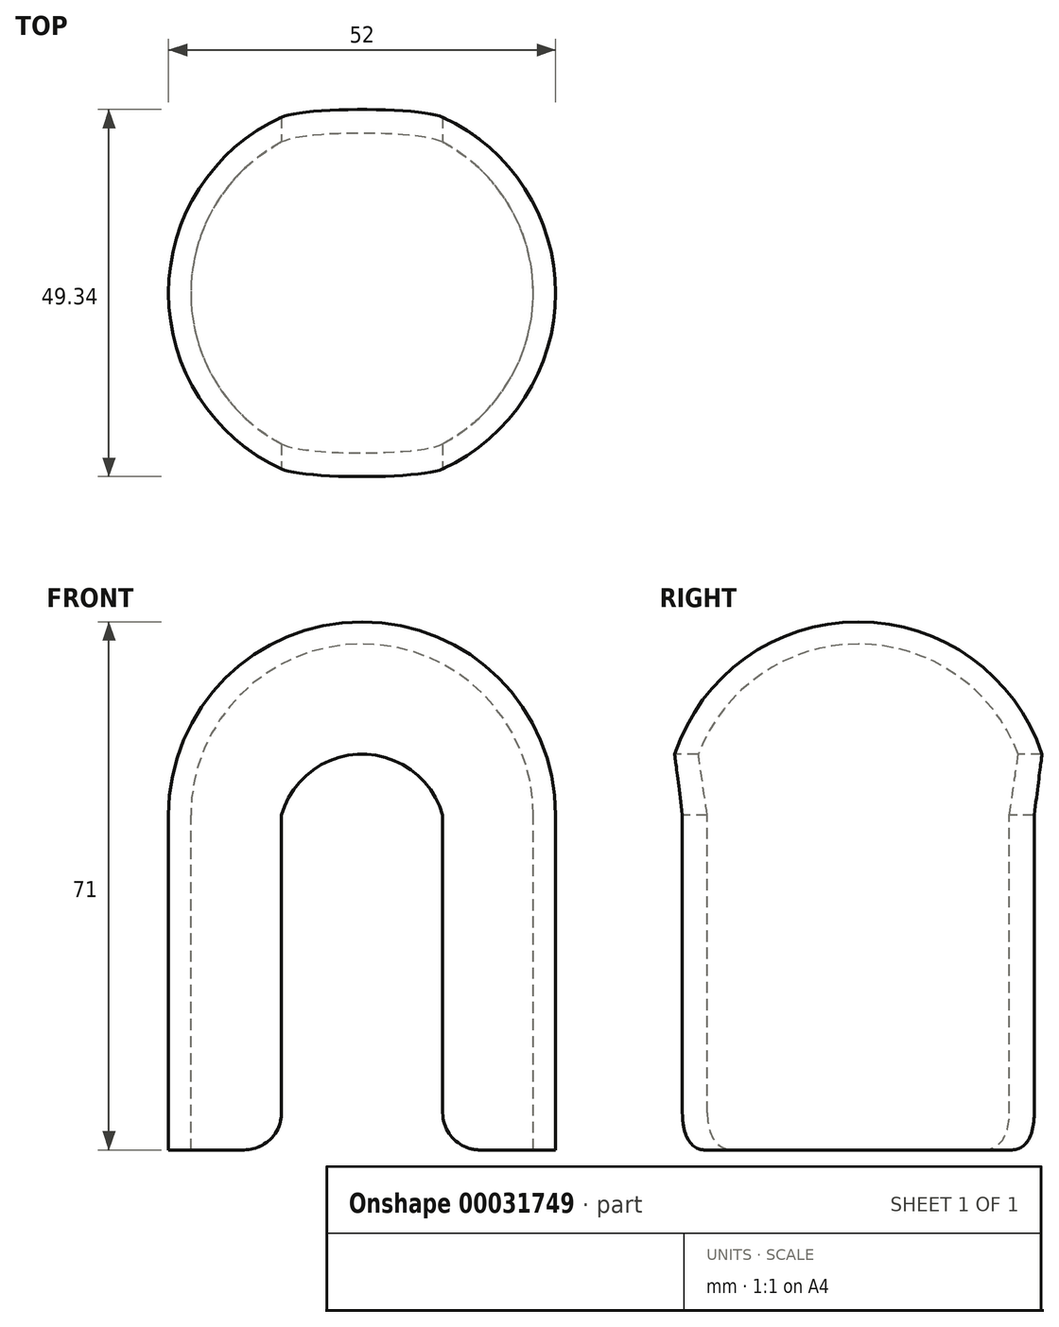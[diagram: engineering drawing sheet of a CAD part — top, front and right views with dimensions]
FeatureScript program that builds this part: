
annotation { "Feature Type Name" : "Feature", "Feature Type Description" : "" }
export const myFeature = defineFeature(function(context is Context, id is Id, definition is map)
    precondition{}
    {
        {
            var Q0;
            Q0=qCreatedBy(makeId("Top.planeOp"),FACE);
            var sketch = newSketch(context, id + "F0", { "sketchPlane" : qUnion([Q0])});
            skLineSegment(sketch, "E0", {"start": v(0, 26) * mm, "end": v(0, -26) * mm});
            skArc(sketch, "E1", {"start": v(0, -26) * mm, "mid": v(26, 0) * mm, "end": v(0, 26) * mm});
            skLineSegment(sketch, "E2", {"start": v(0, 0) * mm, "end": v(24.2, 0) * mm, "construction": true});
            skSolve(sketch);
        }
        {
            var Q0;
            Q0=makeQuery(id+"F0.imprint","IMPRINT",FACE,{"disambiguationData":[TD([[makeQuery(id+"F0.imprint","IMPRINT",EDGE,{"derivedFrom":sQuery(id+"F0.wireOp",EDGE,"E0")}),1.0]])]});
            var Q1;
            Q1=sQuery(id+"F0.wireOp",EDGE,"E0");
            revolve(context, id + "F1", {"entities" : qUnion([Q0]), "axis" : qUnion([Q1]), "revolveType" : RevolveType.ONE_DIRECTION, "angle" : 180 * degree});
        }
        {
            var Q0;
            Q0=qCreatedBy(makeId("Top.planeOp"),FACE);
            var sketch = newSketch(context, id + "F2", { "sketchPlane" : qUnion([Q0])});
            skArc(sketch, "E3", {"start": v(0, -23) * mm, "mid": v(23, 0) * mm, "end": v(0, 23) * mm});
            skLineSegment(sketch, "E4", {"start": v(0, -23) * mm, "end": v(0, 23) * mm});
            skSolve(sketch);
        }
        {
            var Q0;
            Q0 = qSketchRegion(id + "F2", true);
            var Q1;
            Q1=sQuery(id+"F2.wireOp",EDGE,"E4");
            revolve(context, id + "F3", {"operationType" : NewBodyOperationType.REMOVE, "entities" : qUnion([Q0]), "axis" : qUnion([Q1]), "revolveType" : RevolveType.FULL, "oppositeDirection" : true});
        }
        {
            var Q0;
            Q0=qCreatedBy(makeId("Front.planeOp"),FACE);
            cPlane(context, id + "F4", {"entities" : qUnion([Q0]), "cplaneType" : CPlaneType.OFFSET, "offset" : 24.27 * mm, "width" : 150 * mm, "height" : 150 * mm});
        }
        {
            var Q0;
            Q0=qCreatedBy(id+"F4.planeOp",FACE);
            var sketch = newSketch(context, id + "F5", { "sketchPlane" : qUnion([Q0])});
            skCircle(sketch, "E5", {"center": v(0, -3.05) * mm, "radius": 11.25 * mm});
            skArc(sketch, "E6", {"start": v(26, 0) * mm, "mid": v(0, 26) * mm, "end": v(-26, 0) * mm});
            skLineSegment(sketch, "E7", {"start": v(-10.83, 0) * mm, "end": v(10.83, 0) * mm, "construction": true});
            skSolve(sketch);
        }
        {
            var Q0;
            Q0 = qSketchRegion(id + "F5", true);
            extrude(context, id + "F6", {"entities" : qUnion([Q0]), "operationType" : NewBodyOperationType.REMOVE, "oppositeDirection" : true, "depth" : 62.58 * mm, "hasSecondDirection" : true, "secondDirectionOppositeDirection" : false, "secondDirectionDepth" : 22.8 * mm});
        }
        {
            var Q0;
            Q0=makeQuery(id+"F6.boolean.opBoolean","SPLIT",FACE,{"disambiguationData":[OD(1.0)],"derivedFrom":makeQuery(id+"F1.opRevolve","CAP_FACE",FACE,{"disambiguationData":[OSD([sQuery(id+"F0.wireOp",EDGE,"E0"),sQuery(id+"F0.wireOp",EDGE,"E1")])],"isStart":true})});
            var Q1;
            Q1=makeQuery(id+"F6.boolean.opBoolean","SPLIT",FACE,{"disambiguationData":[OD(0.0)],"derivedFrom":makeQuery(id+"F1.opRevolve","CAP_FACE",FACE,{"disambiguationData":[OSD([sQuery(id+"F0.wireOp",EDGE,"E0"),sQuery(id+"F0.wireOp",EDGE,"E1")])],"isStart":true})});
            extrude(context, id + "F7", {"entities" : qUnion([Q0, Q1]), "operationType" : NewBodyOperationType.ADD, "depth" : 45 * mm});
        }
        {
            var Q0;
            {var subQ0=sQuery(id+"F0.wireOp",EDGE,"E0");var subQ1=sQuery(id+"F0.wireOp",EDGE,"E1");var subQ2=sQuery(id+"F5.wireOp",EDGE,"E5");Q0=makeQuery(id+"F7.opExtrude","CAP_EDGE",EDGE,{"disambiguationData":[OSD([subQ0,subQ1,subQ2]),TDD([makeQuery(id+"F6.boolean.opBoolean","INTERSECT",EDGE,{"disambiguationData":[OD(1.0)],"derivedFrom":[makeQuery(id+"F1.opRevolve","CAP_FACE",FACE,{"disambiguationData":[OSD([subQ0,subQ1])],"isStart":true}),makeQuery(id+"F6.opExtrude","SWEPT_FACE",FACE,{"disambiguationData":[OSD([subQ2])]})]})])],"isStart":false});}
            var Q1;
            {var subQ0=sQuery(id+"F0.wireOp",EDGE,"E0");var subQ1=sQuery(id+"F0.wireOp",EDGE,"E1");var subQ2=sQuery(id+"F5.wireOp",EDGE,"E5");Q1=makeQuery(id+"F7.opExtrude","CAP_EDGE",EDGE,{"disambiguationData":[OSD([subQ0,subQ1,subQ2]),TDD([makeQuery(id+"F6.boolean.opBoolean","INTERSECT",EDGE,{"disambiguationData":[OD(3.0)],"derivedFrom":[makeQuery(id+"F1.opRevolve","CAP_FACE",FACE,{"disambiguationData":[OSD([subQ0,subQ1])],"isStart":true}),makeQuery(id+"F6.opExtrude","SWEPT_FACE",FACE,{"disambiguationData":[OSD([subQ2])]})]})])],"isStart":false});}
            var Q2;
            {var subQ0=sQuery(id+"F0.wireOp",EDGE,"E0");var subQ1=sQuery(id+"F0.wireOp",EDGE,"E1");var subQ2=sQuery(id+"F5.wireOp",EDGE,"E5");Q2=makeQuery(id+"F7.opExtrude","CAP_EDGE",EDGE,{"disambiguationData":[OSD([subQ0,subQ1,subQ2]),TDD([makeQuery(id+"F6.boolean.opBoolean","INTERSECT",EDGE,{"disambiguationData":[OD(2.0)],"derivedFrom":[makeQuery(id+"F1.opRevolve","CAP_FACE",FACE,{"disambiguationData":[OSD([subQ0,subQ1])],"isStart":true}),makeQuery(id+"F6.opExtrude","SWEPT_FACE",FACE,{"disambiguationData":[OSD([subQ2])]})]})])],"isStart":false});}
            var Q3;
            {var subQ0=sQuery(id+"F0.wireOp",EDGE,"E0");var subQ1=sQuery(id+"F0.wireOp",EDGE,"E1");var subQ2=sQuery(id+"F5.wireOp",EDGE,"E5");Q3=makeQuery(id+"F7.opExtrude","CAP_EDGE",EDGE,{"disambiguationData":[OSD([subQ0,subQ1,subQ2]),TDD([makeQuery(id+"F6.boolean.opBoolean","INTERSECT",EDGE,{"disambiguationData":[OD(0.0)],"derivedFrom":[makeQuery(id+"F1.opRevolve","CAP_FACE",FACE,{"disambiguationData":[OSD([subQ0,subQ1])],"isStart":true}),makeQuery(id+"F6.opExtrude","SWEPT_FACE",FACE,{"disambiguationData":[OSD([subQ2])]})]})])],"isStart":false});}
            fillet(context, id + "F8", {"entities" : qUnion([Q0, Q1, Q2, Q3]), "radius" : 5 * mm, "tangentPropagation" : true, "allowEdgeOverflow" : false});
        }
    });
